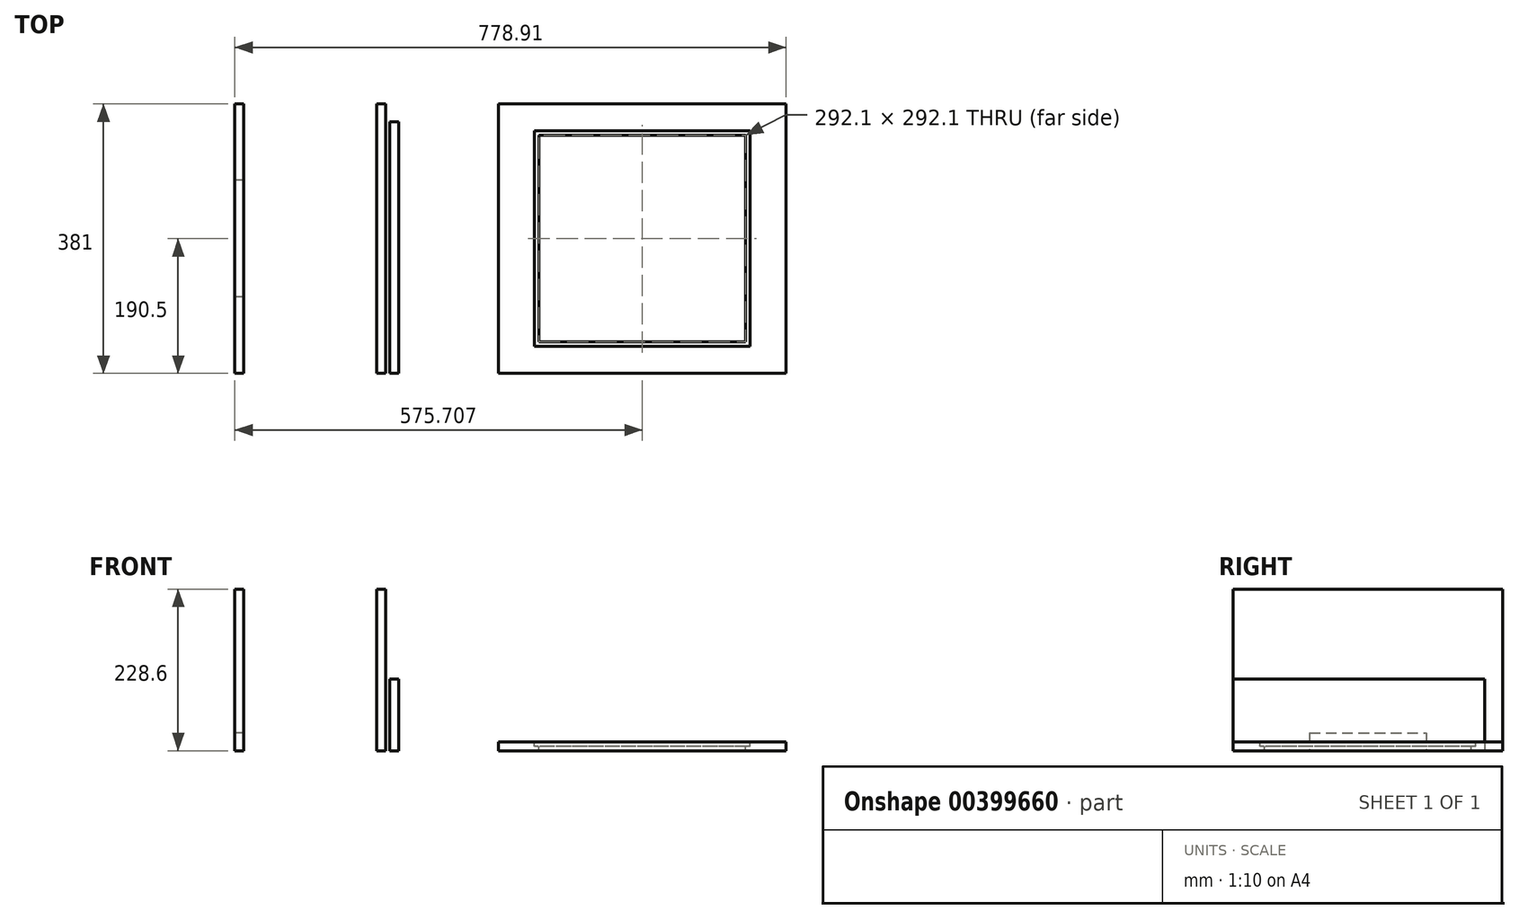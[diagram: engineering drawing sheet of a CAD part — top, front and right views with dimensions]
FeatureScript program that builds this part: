
annotation { "Feature Type Name" : "Feature", "Feature Type Description" : "" }
export const myFeature = defineFeature(function(context is Context, id is Id, definition is map)
    precondition{}
    {
        {
            var Q0;
            Q0=qCreatedBy(makeId("Top.planeOp"),FACE);
            var sketch = newSketch(context, id + "F0", { "sketchPlane" : qUnion([Q0])});
            skLineSegment(sketch, "E0.bottom", {"start": v(0, 0) * mm, "end": v(12.7, 0) * mm});
            skLineSegment(sketch, "E0.top", {"start": v(0, 381) * mm, "end": v(12.7, 381) * mm});
            skLineSegment(sketch, "E0.left", {"start": v(0, 0) * mm, "end": v(0, 381) * mm});
            skLineSegment(sketch, "E0.right", {"start": v(12.7, 0) * mm, "end": v(12.7, 381) * mm});
            skSolve(sketch);
        }
        {
            var Q0;
            Q0 = qSketchRegion(id + "F0", true);
            extrude(context, id + "F1", {"entities" : qUnion([Q0]), "depth" : 228.6 * mm});
        }
        {
            var Q0;
            Q0=qCreatedBy(makeId("Top.planeOp"),FACE);
            var sketch = newSketch(context, id + "F2", { "sketchPlane" : qUnion([Q0])});
            skLineSegment(sketch, "E1.bottom", {"start": v(171.85, 0) * mm, "end": v(578.25, 0) * mm});
            skLineSegment(sketch, "E1.top", {"start": v(171.85, 381) * mm, "end": v(578.25, 381) * mm});
            skLineSegment(sketch, "E1.left", {"start": v(171.85, 0) * mm, "end": v(171.85, 381) * mm});
            skLineSegment(sketch, "E1.right", {"start": v(578.25, 0) * mm, "end": v(578.25, 381) * mm});
            skSolve(sketch);
        }
        {
            var Q0;
            Q0 = qSketchRegion(id + "F2", true);
            extrude(context, id + "F3", {"entities" : qUnion([Q0]), "depth" : 12.7 * mm});
        }
        {
            var Q0;
            Q0=makeQuery(id+"F3.opExtrude","CAP_FACE",FACE,{"disambiguationData":[OSD([sQuery(id+"F2.wireOp",EDGE,"E1.bottom"),sQuery(id+"F2.wireOp",EDGE,"E1.top"),sQuery(id+"F2.wireOp",EDGE,"E1.left"),sQuery(id+"F2.wireOp",EDGE,"E1.right")])],"isStart":false});
            var sketch = newSketch(context, id + "F4", { "sketchPlane" : qUnion([Q0])});
            skLineSegment(sketch, "E2.bottom", {"start": v(527.45, 342.9) * mm, "end": v(222.65, 342.9) * mm});
            skLineSegment(sketch, "E2.top", {"start": v(527.45, 38.1) * mm, "end": v(222.65, 38.1) * mm});
            skLineSegment(sketch, "E2.left", {"start": v(527.45, 342.9) * mm, "end": v(527.45, 38.1) * mm});
            skLineSegment(sketch, "E2.right", {"start": v(222.65, 342.9) * mm, "end": v(222.65, 38.1) * mm});
            skPoint(sketch, "E2.middle", {"position": v(375.05, 190.5) * mm});
            skPoint(sketch, "E2.middle.positionSnap0", {"position": v(171.85, 190.5) * mm});
            skPoint(sketch, "E2.middle.positionSnap1", {"position": v(375.05, 381) * mm});
            skPoint(sketch, "E2.centerSnap0", {"position": v(171.85, 190.5) * mm});
            skPoint(sketch, "E2.centerSnap1", {"position": v(375.05, 381) * mm});
            skSolve(sketch);
        }
        {
            var Q0;
            Q0 = qSketchRegion(id + "F4", true);
            extrude(context, id + "F5", {"entities" : qUnion([Q0]), "operationType" : NewBodyOperationType.REMOVE, "oppositeDirection" : true, "depth" : 6.35 * mm});
        }
        {
            var Q0;
            Q0=makeQuery(id+"F3.opExtrude","CAP_FACE",FACE,{"disambiguationData":[OSD([sQuery(id+"F2.wireOp",EDGE,"E1.bottom"),sQuery(id+"F2.wireOp",EDGE,"E1.top"),sQuery(id+"F2.wireOp",EDGE,"E1.left"),sQuery(id+"F2.wireOp",EDGE,"E1.right")])],"isStart":false});
            var sketch = newSketch(context, id + "F6", { "sketchPlane" : qUnion([Q0])});
            skLineSegment(sketch, "E3.bottom", {"start": v(521.1, 336.55) * mm, "end": v(229, 336.55) * mm});
            skLineSegment(sketch, "E3.top", {"start": v(521.1, 44.45) * mm, "end": v(229, 44.45) * mm});
            skLineSegment(sketch, "E3.left", {"start": v(521.1, 336.55) * mm, "end": v(521.1, 44.45) * mm});
            skLineSegment(sketch, "E3.right", {"start": v(229, 336.55) * mm, "end": v(229, 44.45) * mm});
            skPoint(sketch, "E3.middle", {"position": v(375.05, 190.5) * mm});
            skPoint(sketch, "E3.middle.positionSnap0", {"position": v(222.65, 190.5) * mm});
            skPoint(sketch, "E3.middle.positionSnap1", {"position": v(375.05, 342.9) * mm});
            skPoint(sketch, "E3.centerSnap0", {"position": v(222.65, 190.5) * mm});
            skPoint(sketch, "E3.centerSnap1", {"position": v(375.05, 342.9) * mm});
            skSolve(sketch);
        }
        {
            var Q0;
            Q0 = qSketchRegion(id + "F6", true);
            extrude(context, id + "F7", {"entities" : qUnion([Q0]), "operationType" : NewBodyOperationType.REMOVE, "endBound" : BoundingType.THROUGH_ALL, "oppositeDirection" : true, "depth" : 25.4 * mm});
        }
        {
            var Q0;
            Q0=makeQuery(id+"F1.opExtrude","SWEPT_BODY",BODY,{"disambiguationData":[OSD([sQuery(id+"F0.wireOp",EDGE,"E0.bottom"),sQuery(id+"F0.wireOp",EDGE,"E0.top"),sQuery(id+"F0.wireOp",EDGE,"E0.left"),sQuery(id+"F0.wireOp",EDGE,"E0.right")])]});
            transform(context, id + "F8", {"entities" : qUnion([Q0]), "transformType" : TransformType.TRANSLATION_3D, "dx" : -200.66 * mm, "dy" : 0 * mm, "dz" : 0 * mm, "makeCopy" : true});
        }
        {
            var Q0;
            Q0=makeQuery(id+"F8.opPattern","COPY",FACE,{"derivedFrom":makeQuery(id+"F1.opExtrude","SWEPT_FACE",FACE,{"disambiguationData":[OSD([sQuery(id+"F0.wireOp",EDGE,"E0.left")])]}),"instanceName":"1"});
            var sketch = newSketch(context, id + "F9", { "sketchPlane" : qUnion([Q0])});
            skLineSegment(sketch, "E4.bottom", {"start": v(-107.95, 25.4) * mm, "end": v(-273.05, 25.4) * mm});
            skLineSegment(sketch, "E4.top", {"start": v(-107.95, -25.4) * mm, "end": v(-273.05, -25.4) * mm});
            skLineSegment(sketch, "E4.left", {"start": v(-107.95, 25.4) * mm, "end": v(-107.95, -25.4) * mm});
            skLineSegment(sketch, "E4.right", {"start": v(-273.05, 25.4) * mm, "end": v(-273.05, -25.4) * mm});
            skPoint(sketch, "E4.middle", {"position": v(-190.5, 0) * mm});
            skSolve(sketch);
        }
        {
            var Q0;
            Q0 = qSketchRegion(id + "F9", true);
            extrude(context, id + "F10", {"entities" : qUnion([Q0]), "operationType" : NewBodyOperationType.REMOVE, "oppositeDirection" : true, "depth" : 25.4 * mm});
        }
        {
            var Q0;
            Q0=qCreatedBy(makeId("Top.planeOp"),FACE);
            var sketch = newSketch(context, id + "F11", { "sketchPlane" : qUnion([Q0])});
            skLineSegment(sketch, "E5.bottom", {"start": v(18.3, 0) * mm, "end": v(31, 0) * mm});
            skLineSegment(sketch, "E5.top", {"start": v(18.3, 355.6) * mm, "end": v(31, 355.6) * mm});
            skLineSegment(sketch, "E5.left", {"start": v(18.3, 0) * mm, "end": v(18.3, 355.6) * mm});
            skLineSegment(sketch, "E5.right", {"start": v(31, 0) * mm, "end": v(31, 355.6) * mm});
            skSolve(sketch);
        }
        {
            var Q0;
            Q0 = qSketchRegion(id + "F11", true);
            extrude(context, id + "F12", {"entities" : qUnion([Q0]), "depth" : 101.6 * mm});
        }
    });
